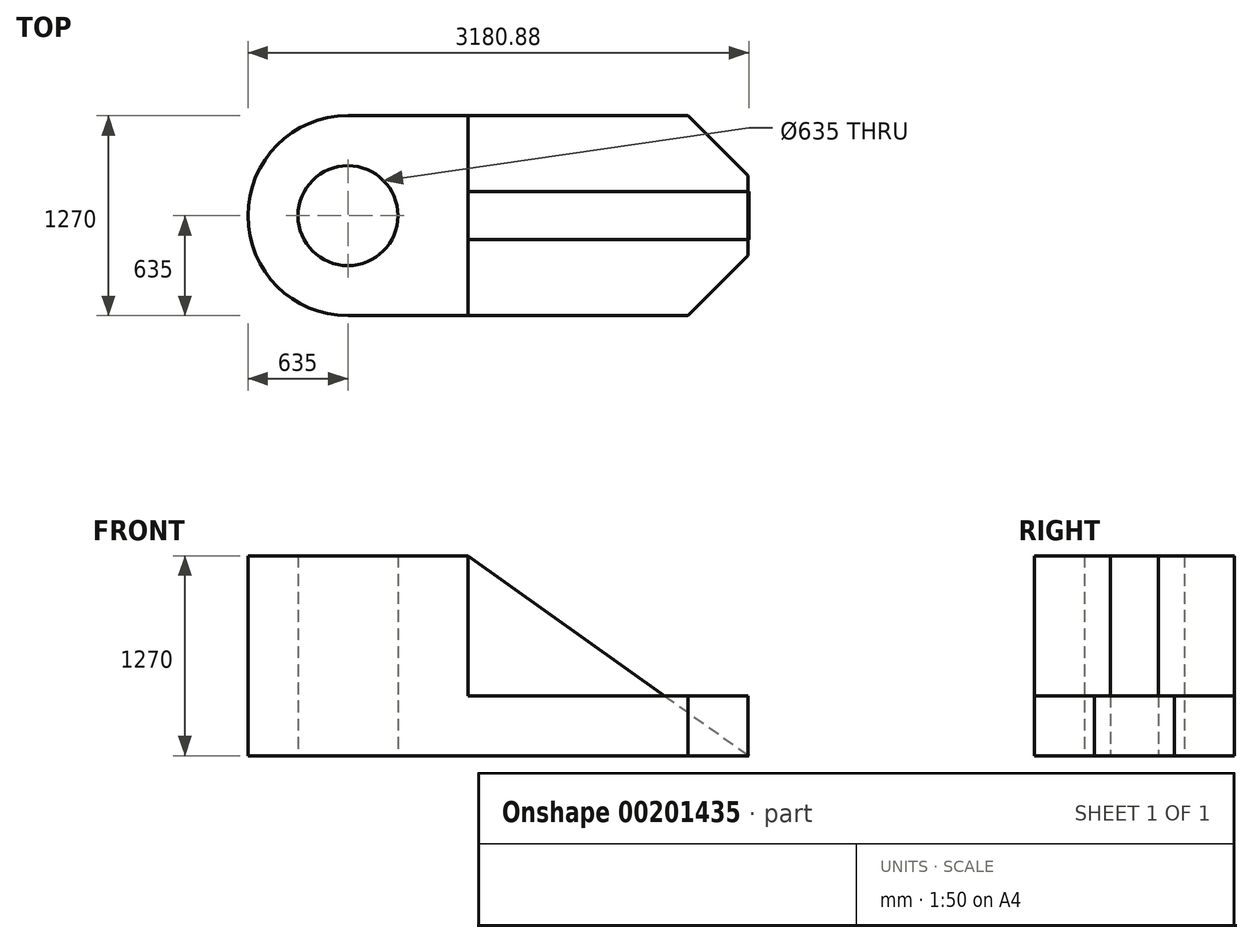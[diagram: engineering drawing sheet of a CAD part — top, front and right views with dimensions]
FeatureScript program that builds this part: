
annotation { "Feature Type Name" : "Feature", "Feature Type Description" : "" }
export const myFeature = defineFeature(function(context is Context, id is Id, definition is map)
    precondition{}
    {
        {
            var Q0;
            Q0=qCreatedBy(makeId("Top.planeOp"),FACE);
            var sketch = newSketch(context, id + "F0", { "sketchPlane" : qUnion([Q0])});
            skLineSegment(sketch, "E0.bottom", {"start": v(0, 0) * mm, "end": v(2159, 0) * mm});
            skLineSegment(sketch, "E0.top", {"start": v(0, 1270) * mm, "end": v(2159, 1270) * mm});
            skArc(sketch, "E1", {"start": v(0, 1270) * mm, "mid": v(-635, 635) * mm, "end": v(0, 0) * mm});
            skLineSegment(sketch, "E2.right", {"start": v(94.73, 1066.14) * mm, "end": v(101.28, 1057.39) * mm, "construction": true});
            skLineSegment(sketch, "E3", {"start": v(2540, 381) * mm, "end": v(2540, 889) * mm});
            skLineSegment(sketch, "E4", {"start": v(2540, 889) * mm, "end": v(2159, 1270) * mm});
            skLineSegment(sketch, "E5", {"start": v(2159, 0) * mm, "end": v(2540, 381) * mm});
            skCircle(sketch, "E6", {"center": v(0, 635) * mm, "radius": 317.5 * mm});
            skLineSegment(sketch, "E7", {"start": v(762, 1270) * mm, "end": v(762, 0) * mm});
            skPoint(sketch, "E7.endSnap0", {"position": v(1079.5, 0) * mm});
            skLineSegment(sketch, "E8", {"start": v(2159, 1270) * mm, "end": v(2540, 1270) * mm, "construction": true});
            skLineSegment(sketch, "E9", {"start": v(2540, 1270) * mm, "end": v(2540, 889) * mm, "construction": true});
            skLineSegment(sketch, "E10", {"start": v(2540, 0) * mm, "end": v(2159, 0) * mm, "construction": true});
            skLineSegment(sketch, "E11", {"start": v(0, 1270) * mm, "end": v(-635, 1270) * mm, "construction": true});
            skPoint(sketch, "E11.endSnap0", {"position": v(-635, 635) * mm});
            skLineSegment(sketch, "E12", {"start": v(-635, 1270) * mm, "end": v(-635, 0) * mm, "construction": true});
            skLineSegment(sketch, "E13", {"start": v(-635, 0) * mm, "end": v(0, 0) * mm, "construction": true});
            skSolve(sketch);
        }
        {
            var Q0;
            {var subQ0=sQuery(id+"F0.wireOp",EDGE,"E1");Q0=makeQuery(id+"F0.imprint","IMPRINT",FACE,{"disambiguationData":[TD([[makeQuery(id+"F0.imprint","IMPRINT",EDGE,{"derivedFrom":subQ0}),1.0]])]});}
            extrude(context, id + "F1", {"entities" : qUnion([Q0]), "depth" : 1270 * mm});
        }
        {
            var Q0;
            Q0 = qSketchRegion(id + "F0", true);
            extrude(context, id + "F2", {"entities" : qUnion([Q0]), "operationType" : NewBodyOperationType.ADD, "depth" : 381 * mm});
        }
        {
            var Q0;
            {var subQ0=sQuery(id+"F0.wireOp",EDGE,"E0.bottom");Q0=makeQuery(id+"F2.boolean.opBoolean","MERGE",FACE,{"derivedFrom":[makeQuery(id+"F1.opExtrude","SWEPT_FACE",FACE,{"disambiguationData":[OSD([subQ0])]}),makeQuery(id+"F2.opExtrude","SWEPT_FACE",FACE,{"disambiguationData":[OSD([subQ0])]})]});}
            var sketch = newSketch(context, id + "F3", { "sketchPlane" : qUnion([Q0])});
            skPoint(sketch, "E14", {"position": v(2545.88, 0) * mm});
            skLineSegment(sketch, "E15", {"start": v(762, 1270) * mm, "end": v(2545.88, 0) * mm});
            skLineSegment(sketch, "E16", {"start": v(2545.88, 0) * mm, "end": v(762, 0) * mm});
            skLineSegment(sketch, "E17", {"start": v(762, 0) * mm, "end": v(762, 1270) * mm});
            skSolve(sketch);
        }
        {
            var Q0;
            {var subQ1=sQuery(id+"F0.wireOp",EDGE,"E0.bottom");var subQ6=sQuery(id+"F3.wireOp",EDGE,"E17");var subQ8=makeQuery(id+"F2.opExtrude","CAP_EDGE",EDGE,{"disambiguationData":[OSD([subQ1])],"isStart":false});var subQ10=makeQuery(id+"F3.imprint","INTERSECT",VERTEX,{"derivedFrom":[subQ8,subQ6]});Q0=makeQuery(id+"F3.imprint","IMPRINT",FACE,{"disambiguationData":[TD([[makeQuery(id+"F3.imprint","IMPRINT",EDGE,{"disambiguationData":[TD([[subQ10,-1.0]])],"derivedFrom":subQ8}),-1.0]])]});}
            var Q1;
            {var subQ0=sQuery(id+"F3.wireOp",EDGE,"E17");var subQ2=sQuery(id+"F0.wireOp",EDGE,"E0.bottom");var subQ4=makeQuery(id+"F2.opExtrude","CAP_EDGE",EDGE,{"disambiguationData":[OSD([subQ2])],"isStart":false});var subQ6=makeQuery(id+"F3.imprint","INTERSECT",VERTEX,{"derivedFrom":[subQ4,subQ0]});Q1=makeQuery(id+"F3.imprint","IMPRINT",FACE,{"disambiguationData":[TD([[makeQuery(id+"F3.imprint","IMPRINT",EDGE,{"disambiguationData":[TD([[subQ6,-1.0]])],"derivedFrom":subQ4}),1.0]])]});}
            var Q2;
            {var subQ0=sQuery(id+"F3.wireOp",EDGE,"E16");var subQ1=sQuery(id+"F3.wireOp",EDGE,"E15");var subQ2=makeQuery(id+"F3.imprint","INTERSECT",VERTEX,{"derivedFrom":[subQ1,subQ0]});Q2=makeQuery(id+"F3.imprint","IMPRINT",FACE,{"disambiguationData":[TD([[makeQuery(id+"F3.imprint","IMPRINT",EDGE,{"disambiguationData":[TD([[subQ2,1.0]])],"derivedFrom":subQ1}),-1.0]])]});}
            extrude(context, id + "F4", {"entities" : qUnion([Q0, Q1, Q2]), "oppositeDirection" : true, "depth" : 787.4 * mm, "hasSecondDirection" : true, "secondDirectionOppositeDirection" : true, "secondDirectionDepth" : 482.6 * mm});
        }
    });
